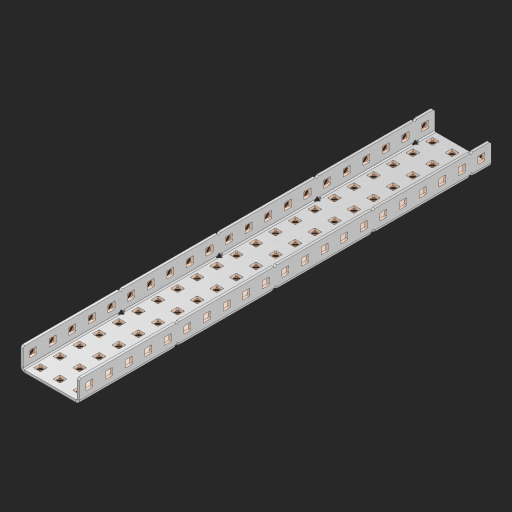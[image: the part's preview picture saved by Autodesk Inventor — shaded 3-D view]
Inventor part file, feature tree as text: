
AUTODESK INVENTOR PART (.ipt)
format: ipt  version: 2023 (Build 270158000, 158)  size: 1,416,704 bytes
history: native  units: in
note: dims shown in document units (in); Inventor stores cm internally (conversion verified against a paired STEP export)
features: other x110, extrude x104, sheet_metal_op x10, sketch x8, mirror x1, pattern_linear x1, chamfer x1
ambient origin geometry x8: Origin, YZ Plane, XZ Plane, XY Plane, X Axis, Y Axis, Z Axis, Center Point
bodies: Solid1 (feature_tree), Body (feature_tree)
feature tree (235):
  other  "Flange Pattern Plane"
  sheet_metal_op  "Flange Pattern"
  sheet_metal_op  "Body Pattern"
  other  "Arc Length"
  mirror  "Notch Mirror"
  pattern_linear  "Notch Pattern"  Spacing1=0.25in  [1 undecoded]
  chamfer  "End Chamfer"
  extrude  "Half Cut"  Depth=0.0625in
  sketch  "Sketch1"  dims[d0=1.5in]
  other  "Plate1"
  sketch  "Sketch2"  dims[d1=10.5in]
  other  "Plate2"
  sheet_metal_op  "Bend1"
  sheet_metal_op  "Corner1"
  sketch  "Sketch3"  dims[d2=0.0625in]
  other  "Flange Pattern Sketch"
  sketch  "Sketch7"  dims[d3=0.0625in]
  other  "Srf1"
  other  "Srf2"
  sketch  "Sketch8"  dims[d4=0.0312in]
  sketch  "Sketch9"  dims[d5=0.125in]
  other  "Srf91"
  sheet_metal_op  "Body Pattern Sketch"
  other  "Srf92"
  sketch  "Sketch13"  dims[d6=0.0625in]
  sketch  "Sketch14"  dims[d7=0.5in d8=90.0deg d9=0.0312in d10=0.25in d11=0.0625in d12=0.0625in d16=0.182in d17=0.02in d18=0.0625in d19=0.0in d20=0.25in d21=0.25in d46=0.172in d47=1.0in d48=0.0in d49=0.182in d50=0.02in d51=0.25in d52=0.25in d53=0.0625in d54=0.0in d55=0.172in d56=1.0in d57=0.0in d60=8.2677in d62=0.5in d63=1.1811in d65=0.5in d85=0.1473in d86=0.1782in d88=0.04in d89=0.0625in d90=0.0in d91=0.04in d92=0.0491in d95=2.5in d96=0.04in d97=0.25in d98=45.0deg d101=0.0in d102=2.497in d131=1.5in d132=8.2677in d134=0.5in d139=0.5in]
  other  "Srf856"
  other  "Srf1310"
  other  "Srf1311"
  other  "Srf1312"
  other  "Srf1376"
  other  "Srf1377"
  other  "Srf1728"
  other  "Srf1755"
  other  "Srf1878"
  other  "Srf1879"
  other  "Srf1880"
  other  "Srf1881"
  other  "Srf1882"
  other  "Srf1883"
  other  "Srf1884"
  other  "Srf1885"
  other  "Srf1886"
  other  "Srf1887"
  other  "Srf1888"
  other  "Srf1889"
  other  "Srf1890"
  other  "Srf1891"
  other  "Srf1892"
  other  "Srf1893"
  other  "Srf1894"
  other  "Srf1895"
  other  "Srf1896"
  other  "Srf1897"
  other  "Srf1898"
  other  "Srf1899"
  other  "Srf1900"
  other  "Srf1901"
  other  "Srf1902"
  other  "Srf1903"
  other  "Srf1904"
  other  "Srf1905"
  other  "Srf1906"
  other  "Srf1907"
  other  "Srf1908"
  other  "Srf1909"
  other  "Srf1910"
  other  "Srf1911"
  other  "Srf1912"
  other  "Srf1913"
  other  "Srf1942"
  other  "Srf1943"
  other  "Srf1944"
  other  "Srf1945"
  other  "Srf1946"
  other  "Srf1947"
  other  "Srf1948"
  other  "Srf1949"
  other  "Srf1950"
  other  "Srf1951"
  other  "Srf1952"
  other  "Srf1953"
  other  "Srf1954"
  other  "Srf1955"
  other  "Srf1956"
  other  "Srf1957"
  other  "Srf1958"
  other  "Srf1959"
  other  "Srf1960"
  other  "Srf1961"
  other  "Srf1962"
  other  "Srf1963"
  other  "Srf1964"
  other  "Srf1965"
  other  "Srf1966"
  other  "Srf1967"
  other  "Srf1968"
  other  "Srf1969"
  other  "Srf1970"
  other  "Srf1971"
  other  "Srf1972"
  other  "Srf1973"
  other  "Srf1974"
  other  "Srf1975"
  other  "Srf1976"
  other  "Srf1977"
  other  "Srf1978"
  other  "Srf1979"
  other  "Srf1980"
  other  "Srf1981"
  other  "Srf1982"
  other  "Srf1983"
  other  "Srf1984"
  other  "Srf1985"
  other  "Srf1986"
  other  "Srf1987"
  other  "Srf1988"
  other  "Srf1989"
  other  "Srf1990"
  other  "Srf1991"
  other  "Srf1992"
  other  "Srf1993"
  other  "Srf1994"
  other  "Srf1995"
  other  "Srf1996"
  other  "Srf1997"
  other  "Srf1998"
  sheet_metal_op  "Flange Stamp"
  sheet_metal_op  "Flange Circle"
  sheet_metal_op  "Body Stamp"
  sheet_metal_op  "Body Circle"
  sheet_metal_op  "Notch"
  extrude  "ExtrusionSrf2"  Depth=0.0625in
  extrude  "ExtrusionSrf92"  Depth=1.5in
  extrude  "ExtrusionSrf856"  Depth=0.02in
  extrude  "ExtrusionSrf1310"  Depth=0.0625in
  extrude  "ExtrusionSrf1311"  TaperAngle=0.0deg  [1 undecoded]
  extrude  "ExtrusionSrf1312"  Depth=0.25in
  extrude  "ExtrusionSrf1376"  Depth=0.25in
  extrude  "ExtrusionSrf1377"  Depth=1.5in
  extrude  "ExtrusionSrf1728"  Depth=1.5in TaperAngle=0.0deg
  extrude  "ExtrusionSrf1755"  Depth=1.5in
  extrude  "ExtrusionSrf1878"  Depth=0.02in
  extrude  "ExtrusionSrf1879"  Depth=0.25in
  extrude  "ExtrusionSrf1880"  Depth=0.25in
  extrude  "ExtrusionSrf1881"  Depth=0.0625in
  extrude  "ExtrusionSrf1882"  TaperAngle=0.0deg  [1 undecoded]
  extrude  "ExtrusionSrf1883"  Depth=1.5in
  extrude  "ExtrusionSrf1884"  Depth=1.5in TaperAngle=0.0deg
  extrude  "ExtrusionSrf1885"  Depth=1.5in
  extrude  "ExtrusionSrf1886"  Depth=1.5in
  extrude  "ExtrusionSrf1887"  Depth=1.5in
  extrude  "ExtrusionSrf1888"  Depth=1.5in
  extrude  "ExtrusionSrf1889"  Depth=1.5in
  extrude  "ExtrusionSrf1890"  Depth=0.0625in
  extrude  "ExtrusionSrf1891"  TaperAngle=0.0deg  [1 undecoded]
  extrude  "ExtrusionSrf1892"  Depth=1.5in
  extrude  "ExtrusionSrf1893"  Depth=1.5in
  extrude  "ExtrusionSrf1894"  Depth=1.5in
  extrude  "ExtrusionSrf1895"  Depth=0.25in TaperAngle=45.0deg
  extrude  "ExtrusionSrf1896"  TaperAngle=0.0deg  [1 undecoded]
  extrude  "ExtrusionSrf1897"  Depth=1.5in
  extrude  "ExtrusionSrf1898"  Depth=1.5in
  extrude  "ExtrusionSrf1899"  Depth=1.5in
  extrude  "ExtrusionSrf1900"  Depth=1.5in
  extrude  "ExtrusionSrf1901"  Depth=1.5in
  extrude  "ExtrusionSrf1902"  [1 undecoded]
  extrude  "ExtrusionSrf1903"  [1 undecoded]
  extrude  "ExtrusionSrf1904"  [1 undecoded]
  extrude  "ExtrusionSrf1905"  [1 undecoded]
  extrude  "ExtrusionSrf1906"  [1 undecoded]
  extrude  "ExtrusionSrf1907"  [1 undecoded]
  extrude  "ExtrusionSrf1908"  [1 undecoded]
  extrude  "ExtrusionSrf1909"  [1 undecoded]
  extrude  "ExtrusionSrf1910"  [1 undecoded]
  extrude  "ExtrusionSrf1911"  [1 undecoded]
  extrude  "ExtrusionSrf1912"  [1 undecoded]
  extrude  "ExtrusionSrf1913"  [1 undecoded]
  extrude  "ExtrusionSrf1942"  [1 undecoded]
  extrude  "ExtrusionSrf1943"  [1 undecoded]
  extrude  "ExtrusionSrf1944"  [1 undecoded]
  extrude  "ExtrusionSrf1945"  [1 undecoded]
  extrude  "ExtrusionSrf1946"  [1 undecoded]
  extrude  "ExtrusionSrf1947"  [1 undecoded]
  extrude  "ExtrusionSrf1948"  [1 undecoded]
  extrude  "ExtrusionSrf1949"  [1 undecoded]
  extrude  "ExtrusionSrf1950"  [1 undecoded]
  extrude  "ExtrusionSrf1951"  [1 undecoded]
  extrude  "ExtrusionSrf1952"  [1 undecoded]
  extrude  "ExtrusionSrf1953"  [1 undecoded]
  extrude  "ExtrusionSrf1954"  [1 undecoded]
  extrude  "ExtrusionSrf1955"  [1 undecoded]
  extrude  "ExtrusionSrf1956"  [1 undecoded]
  extrude  "ExtrusionSrf1957"  [1 undecoded]
  extrude  "ExtrusionSrf1958"  [1 undecoded]
  extrude  "ExtrusionSrf1959"  [1 undecoded]
  extrude  "ExtrusionSrf1960"  [1 undecoded]
  extrude  "ExtrusionSrf1961"  [1 undecoded]
  extrude  "ExtrusionSrf1962"  [1 undecoded]
  extrude  "ExtrusionSrf1963"  [1 undecoded]
  extrude  "ExtrusionSrf1964"  [1 undecoded]
  extrude  "ExtrusionSrf1965"  [1 undecoded]
  extrude  "ExtrusionSrf1966"  [1 undecoded]
  extrude  "ExtrusionSrf1967"  [1 undecoded]
  extrude  "ExtrusionSrf1968"  [1 undecoded]
  extrude  "ExtrusionSrf1969"  [1 undecoded]
  extrude  "ExtrusionSrf1970"  [1 undecoded]
  extrude  "ExtrusionSrf1971"  [1 undecoded]
  extrude  "ExtrusionSrf1972"  [1 undecoded]
  extrude  "ExtrusionSrf1973"  [1 undecoded]
  extrude  "ExtrusionSrf1974"  [1 undecoded]
  extrude  "ExtrusionSrf1975"  [1 undecoded]
  extrude  "ExtrusionSrf1976"  [1 undecoded]
  extrude  "ExtrusionSrf1977"  [1 undecoded]
  extrude  "ExtrusionSrf1978"  [1 undecoded]
  extrude  "ExtrusionSrf1979"  [1 undecoded]
  extrude  "ExtrusionSrf1980"  [1 undecoded]
  extrude  "ExtrusionSrf1981"  [1 undecoded]
  extrude  "ExtrusionSrf1982"  [1 undecoded]
  extrude  "ExtrusionSrf1983"  [1 undecoded]
  extrude  "ExtrusionSrf1984"  [1 undecoded]
  extrude  "ExtrusionSrf1985"  [1 undecoded]
  extrude  "ExtrusionSrf1986"  [1 undecoded]
  extrude  "ExtrusionSrf1987"  [1 undecoded]
  extrude  "ExtrusionSrf1988"  [1 undecoded]
  extrude  "ExtrusionSrf1989"  [1 undecoded]
  extrude  "ExtrusionSrf1990"  [1 undecoded]
  extrude  "ExtrusionSrf1991"  [1 undecoded]
  extrude  "ExtrusionSrf1992"  [1 undecoded]
  extrude  "ExtrusionSrf1993"  [1 undecoded]
  extrude  "ExtrusionSrf1994"  [1 undecoded]
  extrude  "ExtrusionSrf1995"  [1 undecoded]
  extrude  "ExtrusionSrf1996"  [1 undecoded]
  extrude  "ExtrusionSrf1997"  [1 undecoded]
  extrude  "ExtrusionSrf1998"  [1 undecoded]
note: 74 required parameter values undecoded (feature->parameter linkage not recoverable at this tier; creation-order binding heuristic only, values carry confidence <= 0.55)
